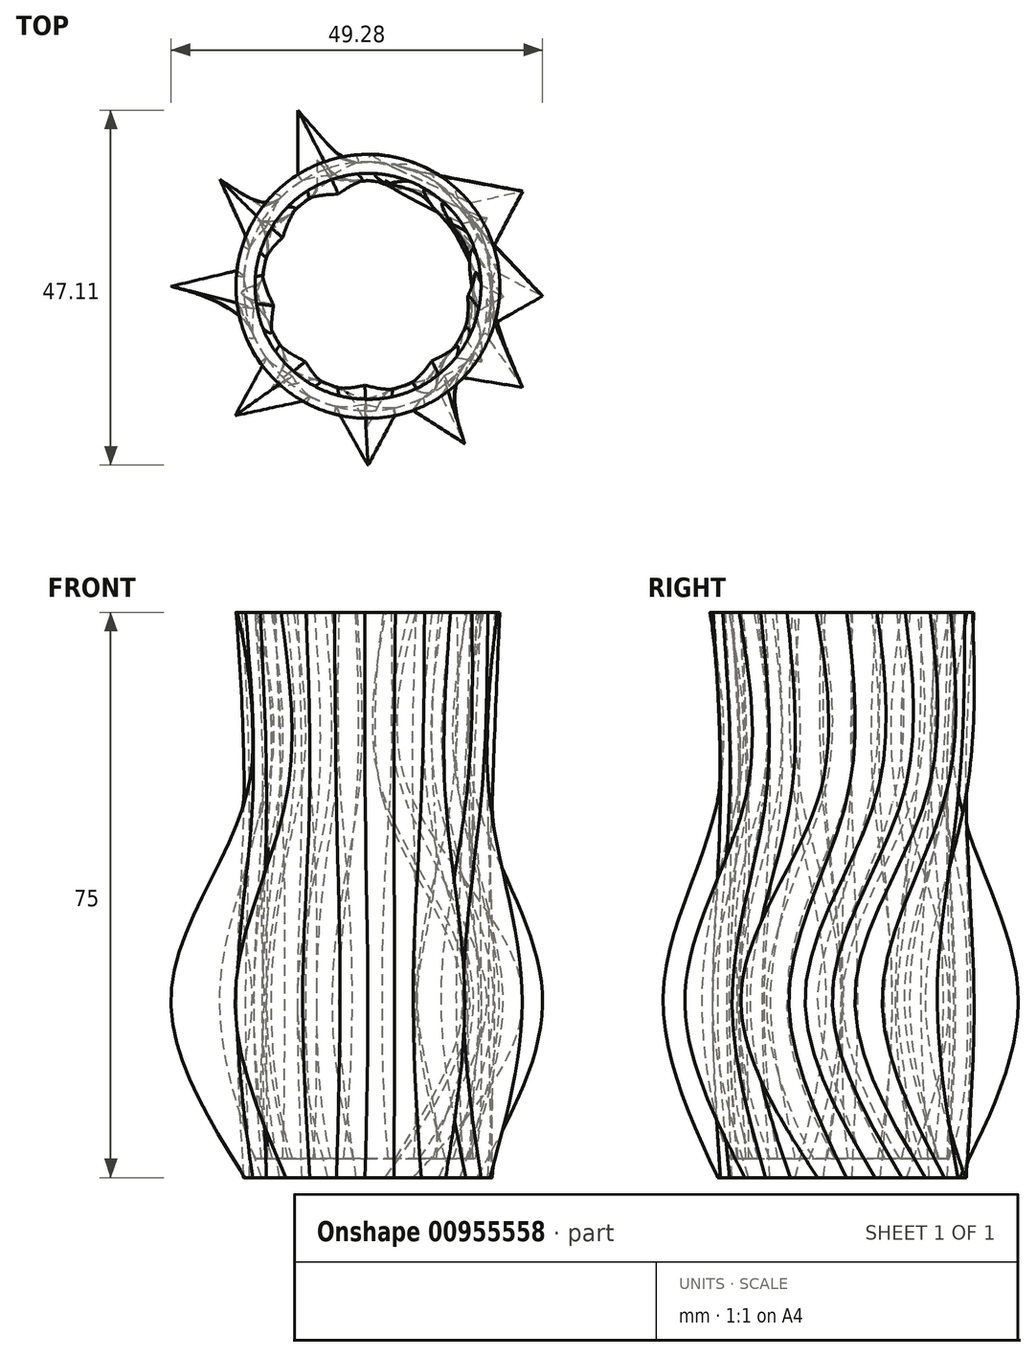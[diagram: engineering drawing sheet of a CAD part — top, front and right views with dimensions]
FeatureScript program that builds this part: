
annotation { "Feature Type Name" : "Feature", "Feature Type Description" : "" }
export const myFeature = defineFeature(function(context is Context, id is Id, definition is map)
    precondition{}
    {
        {
            var Q0;
            Q0=qCreatedBy(makeId("Top.planeOp"),FACE);
            var sketch = newSketch(context, id + "F0", { "sketchPlane" : qUnion([Q0])});
            skLineSegment(sketch, "E0", {"start": v(12.1, 11.32) * mm, "end": v(20.12, 14.4) * mm});
            skLineSegment(sketch, "E1", {"start": v(15.87, 4.53) * mm, "end": v(20.12, 14.4) * mm});
            skLineSegment(sketch, "E2", {"start": v(17.15, 0) * mm, "end": v(28.28, -5.03) * mm});
            skLineSegment(sketch, "E3", {"start": v(15.7, -6.88) * mm, "end": v(28.28, -5.03) * mm});
            skLineSegment(sketch, "E4", {"start": v(9.6, -14.21) * mm, "end": v(22.3, -23.54) * mm});
            skLineSegment(sketch, "E5", {"start": v(22.3, -23.54) * mm, "end": v(15.82, -6.62) * mm});
            skLineSegment(sketch, "E6", {"start": v(0, -17.15) * mm, "end": v(5.66, -26.4) * mm});
            skLineSegment(sketch, "E7", {"start": v(7.05, -15.63) * mm, "end": v(5.66, -26.4) * mm});
            skLineSegment(sketch, "E8", {"start": v(-9.03, -14.58) * mm, "end": v(-9.03, -29.16) * mm});
            skLineSegment(sketch, "E9", {"start": v(-2.88, -16.9) * mm, "end": v(-9.03, -29.16) * mm});
            skLineSegment(sketch, "E10", {"start": v(-12.66, -11.57) * mm, "end": v(-26.36, -16.83) * mm});
            skLineSegment(sketch, "E11", {"start": v(-16.66, -4.07) * mm, "end": v(-26.36, -16.83) * mm});
            skLineSegment(sketch, "E12", {"start": v(-17.03, 1.96) * mm, "end": v(-26.36, 12.57) * mm});
            skLineSegment(sketch, "E13", {"start": v(-14.92, 8.45) * mm, "end": v(-26.36, 12.57) * mm});
            skLineSegment(sketch, "E14", {"start": v(-11, 13.15) * mm, "end": v(-11, 26.9) * mm});
            skLineSegment(sketch, "E15", {"start": v(-4.16, 16.64) * mm, "end": v(-11, 26.9) * mm});
            skLineSegment(sketch, "E16", {"start": v(3.05, 16.87) * mm, "end": v(7.67, 26.9) * mm});
            skLineSegment(sketch, "E17", {"start": v(11.66, 12.57) * mm, "end": v(7.67, 26.9) * mm});
            skCircle(sketch, "E18", {"center": v(0, 0) * mm, "radius": 16.5 * mm});
            skSolve(sketch);
        }
        {
            var Q0;
            Q0=qCreatedBy(makeId("Top.planeOp"),FACE);
            cPlane(context, id + "F1", {"entities" : qUnion([Q0]), "cplaneType" : CPlaneType.OFFSET, "offset" : 25 * mm, "width" : 150 * mm, "height" : 150 * mm});
        }
        {
            var Q0;
            Q0=qCreatedBy(id+"F1.planeOp",FACE);
            var sketch = newSketch(context, id + "F2", { "sketchPlane" : qUnion([Q0])});
            skCircle(sketch, "E19", {"center": v(0, 0) * mm, "radius": 17.5 * mm});
            skLineSegment(sketch, "E20", {"start": v(-9.28, 14.84) * mm, "end": v(-9.28, 23.34) * mm});
            skLineSegment(sketch, "E21", {"start": v(-3.8, 17.08) * mm, "end": v(-9.28, 23.34) * mm});
            skLineSegment(sketch, "E22", {"start": v(3.4, 17.17) * mm, "end": v(7.55, 23.34) * mm});
            skLineSegment(sketch, "E23", {"start": v(8.74, 15.36) * mm, "end": v(7.55, 23.34) * mm});
            skLineSegment(sketch, "E24", {"start": v(13.5, 11.13) * mm, "end": v(20.45, 12.64) * mm});
            skLineSegment(sketch, "E25", {"start": v(16.65, 5.38) * mm, "end": v(20.45, 12.64) * mm});
            skLineSegment(sketch, "E26", {"start": v(17.41, 1.75) * mm, "end": v(23.12, -1.23) * mm});
            skLineSegment(sketch, "E27", {"start": v(16.82, -4.84) * mm, "end": v(23.12, -1.23) * mm});
            skLineSegment(sketch, "E28", {"start": v(12.65, -12.09) * mm, "end": v(20.45, -13.32) * mm});
            skLineSegment(sketch, "E29", {"start": v(20.45, -13.32) * mm, "end": v(16.05, -6.98) * mm});
            skLineSegment(sketch, "E30", {"start": v(9.73, -14.54) * mm, "end": v(12.81, -20.8) * mm});
            skLineSegment(sketch, "E31", {"start": v(6, -16.44) * mm, "end": v(12.81, -20.8) * mm});
            skLineSegment(sketch, "E32", {"start": v(0, -23.68) * mm, "end": v(3.55, -17.14) * mm});
            skLineSegment(sketch, "E33", {"start": v(0, -23.68) * mm, "end": v(-3.7, -17.1) * mm});
            skLineSegment(sketch, "E34", {"start": v(-8.65, -15.21) * mm, "end": v(-17.57, -17.1) * mm});
            skLineSegment(sketch, "E35", {"start": v(-17.57, -17.1) * mm, "end": v(-13.99, -10.52) * mm});
            skLineSegment(sketch, "E36", {"start": v(-17.37, -2.09) * mm, "end": v(-26.05, 0) * mm});
            skLineSegment(sketch, "E37", {"start": v(-17.37, 2.09) * mm, "end": v(-26.05, 0) * mm});
            skLineSegment(sketch, "E38", {"start": v(-16.19, 6.65) * mm, "end": v(-19.6, 14.17) * mm});
            skLineSegment(sketch, "E39", {"start": v(-13.99, 10.52) * mm, "end": v(-19.6, 14.17) * mm});
            skSolve(sketch);
        }
        {
            var Q0;
            Q0=qCreatedBy(id+"F1.planeOp",FACE);
            cPlane(context, id + "F3", {"entities" : qUnion([Q0]), "cplaneType" : CPlaneType.OFFSET, "offset" : 25 * mm, "width" : 150 * mm, "height" : 150 * mm});
        }
        {
            var Q0;
            Q0=qCreatedBy(id+"F3.planeOp",FACE);
            var sketch = newSketch(context, id + "F4", { "sketchPlane" : qUnion([Q0])});
            skCircle(sketch, "E40", {"center": v(0, 0) * mm, "radius": 16.5 * mm});
            skSolve(sketch);
        }
        {
            var Q0;
            Q0=qCreatedBy(id+"F3.planeOp",FACE);
            cPlane(context, id + "F5", {"entities" : qUnion([Q0]), "cplaneType" : CPlaneType.OFFSET, "offset" : 25 * mm, "width" : 150 * mm, "height" : 150 * mm});
        }
        {
            var Q0;
            Q0=qCreatedBy(id+"F5.planeOp",FACE);
            var sketch = newSketch(context, id + "F6", { "sketchPlane" : qUnion([Q0])});
            skCircle(sketch, "E41", {"center": v(0, 0) * mm, "radius": 17.5 * mm});
            skSolve(sketch);
        }
        {
            var Q0;
            {var subQ0=sQuery(id+"F0.wireOp",EDGE,"E18");Q0=makeQuery(id+"F0.imprint","IMPRINT",FACE,{"disambiguationData":[TD([[makeQuery(id+"F0.imprint","IMPRINT",EDGE,{"disambiguationData":[TD([[makeQuery(id+"F0.imprint","IMPRINT",VERTEX,{"derivedFrom":subQ0}),-1.0]])],"derivedFrom":subQ0}),1.0]])]});}
            var Q1;
            Q1 = qSketchRegion(id + "F2", true);
            var Q2;
            Q2 = qSketchRegion(id + "F4", true);
            var Q3;
            Q3 = qSketchRegion(id + "F6", true);
            loft(context, id + "F7", {"sheetProfilesArray" : [{ "sheetProfileEntities" : qUnion([Q0]) }, { "sheetProfileEntities" : qUnion([Q1]) }, { "sheetProfileEntities" : qUnion([Q2]) }, { "sheetProfileEntities" : qUnion([Q3]) }]});
        }
        {
            var Q0;
            Q0=makeQuery(id+"F7.opLoft","CAP_FACE",FACE,{"disambiguationData":[OSD([makeQuery(id+"F6.imprint","IMPRINT",FACE,{"disambiguationData":[TD([[makeQuery(id+"F6.imprint","IMPRINT",EDGE,{"derivedFrom":sQuery(id+"F6.wireOp",EDGE,"E41")}),1.0]])]})])],"isStart":true});
            shell(context, id + "F8", {"entities" : qUnion([Q0]), "thickness" : 2.5 * mm});
        }
    });
